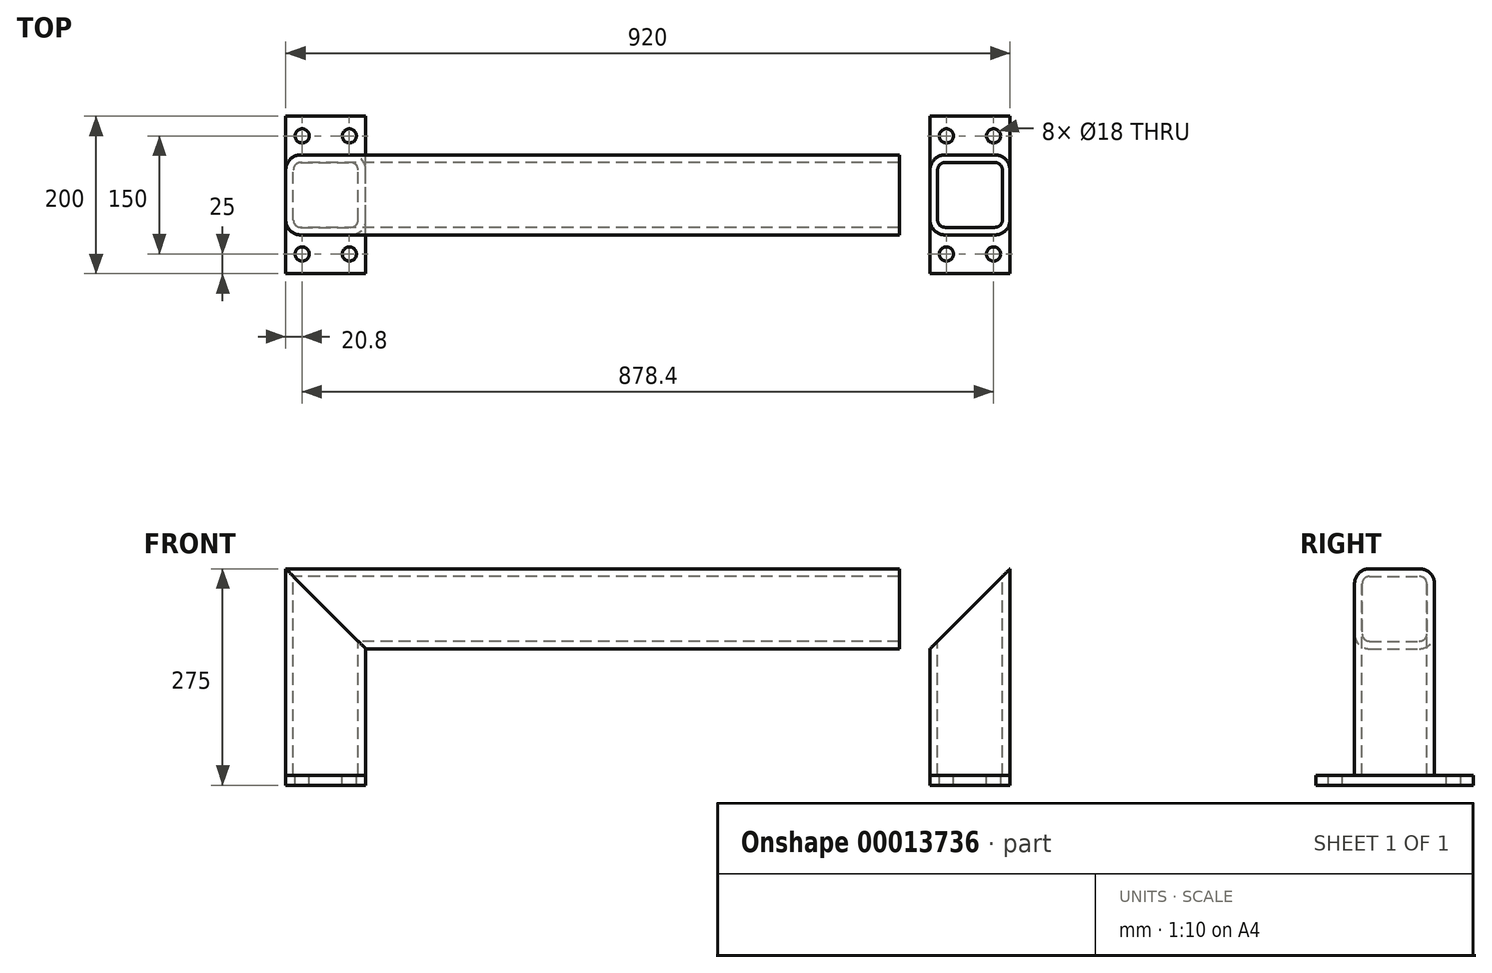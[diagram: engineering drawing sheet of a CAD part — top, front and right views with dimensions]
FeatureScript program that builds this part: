
annotation { "Feature Type Name" : "Feature", "Feature Type Description" : "" }
export const myFeature = defineFeature(function(context is Context, id is Id, definition is map)
    precondition{}
    {
        {
            var Q0;
            Q0=qCreatedBy(makeId("Right.planeOp"),FACE);
            var sketch = newSketch(context, id + "F0", { "sketchPlane" : qUnion([Q0])});
            skLineSegment(sketch, "E0.rect.bottom", {"start": v(-31.8, 50.8) * mm, "end": v(31.8, 50.8) * mm});
            skLineSegment(sketch, "E0.rect.top", {"start": v(-31.8, -50.8) * mm, "end": v(31.8, -50.8) * mm});
            skLineSegment(sketch, "E0.rect.left", {"start": v(-50.8, 31.8) * mm, "end": v(-50.8, -31.8) * mm});
            skLineSegment(sketch, "E0.rect.right", {"start": v(50.8, 31.8) * mm, "end": v(50.8, -31.8) * mm});
            skPoint(sketch, "E0.rect.middle", {"position": v(0, 0) * mm});
            skPoint(sketch, "E1.visualSharp", {"position": v(-50.8, 50.8) * mm});
            skArc(sketch, "E1.filletArc", {"start": v(-31.8, 50.8) * mm, "mid": v(-45.24, 45.24) * mm, "end": v(-50.8, 31.8) * mm});
            skPoint(sketch, "E2.visualSharp", {"position": v(50.8, 50.8) * mm});
            skArc(sketch, "E2.filletArc", {"start": v(50.8, 31.8) * mm, "mid": v(45.24, 45.24) * mm, "end": v(31.8, 50.8) * mm});
            skPoint(sketch, "E3.visualSharp", {"position": v(50.8, -50.8) * mm});
            skArc(sketch, "E3.filletArc", {"start": v(31.8, -50.8) * mm, "mid": v(45.24, -45.24) * mm, "end": v(50.8, -31.8) * mm});
            skPoint(sketch, "E4.visualSharp", {"position": v(-50.8, -50.8) * mm});
            skArc(sketch, "E4.filletArc", {"start": v(-50.8, -31.8) * mm, "mid": v(-45.24, -45.24) * mm, "end": v(-31.8, -50.8) * mm});
            skArc(sketch, "E5.0", {"start": v(-31.8, 41.15) * mm, "mid": v(-38.41, 38.41) * mm, "end": v(-41.15, 31.8) * mm});
            skLineSegment(sketch, "E5.1", {"start": v(-41.15, 31.8) * mm, "end": v(-41.15, -31.8) * mm});
            skArc(sketch, "E5.2", {"start": v(-41.15, -31.8) * mm, "mid": v(-38.41, -38.41) * mm, "end": v(-31.8, -41.15) * mm});
            skLineSegment(sketch, "E5.3", {"start": v(-31.8, -41.15) * mm, "end": v(31.8, -41.15) * mm});
            skArc(sketch, "E5.4", {"start": v(31.8, -41.15) * mm, "mid": v(38.41, -38.41) * mm, "end": v(41.15, -31.8) * mm});
            skLineSegment(sketch, "E5.5", {"start": v(-31.8, 41.15) * mm, "end": v(31.8, 41.15) * mm});
            skLineSegment(sketch, "E5.6", {"start": v(41.15, 31.8) * mm, "end": v(41.15, -31.8) * mm});
            skArc(sketch, "E5.7", {"start": v(41.15, 31.8) * mm, "mid": v(38.41, 38.41) * mm, "end": v(31.8, 41.15) * mm});
            skSolve(sketch);
        }
        {
            var Q0;
            Q0 = qSketchRegion(id + "F0", true);
            extrude(context, id + "F1", {"entities" : qUnion([Q0]), "endBound" : BoundingType.SYMMETRIC, "depth" : 920 * mm});
        }
        {
            var Q0;
            Q0=makeQuery(id+"F1.opExtrude","SWEPT_FACE",FACE,{"disambiguationData":[OSD([sQuery(id+"F0.wireOp",EDGE,"E0.rect.right")])]});
            var sketch = newSketch(context, id + "F2", { "sketchPlane" : qUnion([Q0])});
            skLineSegment(sketch, "E6.0", {"start": v(-460, 50.8) * mm, "end": v(460, 50.8) * mm, "construction": true});
            skLineSegment(sketch, "E7.0", {"start": v(-460, -50.8) * mm, "end": v(460, -50.8) * mm, "construction": true});
            skLineSegment(sketch, "E8", {"start": v(-460, 50.8) * mm, "end": v(-332.27, -76.93) * mm});
            skLineSegment(sketch, "E9.0", {"start": v(-460, 31.8) * mm, "end": v(-460, -31.8) * mm});
            skLineSegment(sketch, "E10", {"start": v(-332.27, -76.93) * mm, "end": v(-460, -76.93) * mm});
            skLineSegment(sketch, "E11", {"start": v(-460, -76.93) * mm, "end": v(-460, 50.8) * mm});
            skLineSegment(sketch, "E12", {"start": v(0, 0) * mm, "end": v(0, -179.73) * mm, "construction": true});
            skLineSegment(sketch, "E13.0.MirrorCS", {"start": v(460, -76.93) * mm, "end": v(460, 50.8) * mm});
            skLineSegment(sketch, "E13.1.MirrorCS", {"start": v(460, 50.8) * mm, "end": v(332.27, -76.93) * mm});
            skLineSegment(sketch, "E13.2.MirrorCS", {"start": v(460, 31.8) * mm, "end": v(460, -31.8) * mm});
            skLineSegment(sketch, "E13.3.MirrorCS", {"start": v(332.27, -76.93) * mm, "end": v(460, -76.93) * mm});
            skSolve(sketch);
        }
        {
            var Q0;
            Q0 = qSketchRegion(id + "F2", true);
            extrude(context, id + "F3", {"entities" : qUnion([Q0]), "operationType" : NewBodyOperationType.REMOVE, "endBound" : BoundingType.THROUGH_ALL, "oppositeDirection" : true, "depth" : 25 * mm});
        }
        {
            var Q0;
            Q0=makeQuery(id+"F1.opExtrude","SWEPT_FACE",FACE,{"disambiguationData":[OSD([sQuery(id+"F0.wireOp",EDGE,"E0.rect.bottom")])]});
            var sketch = newSketch(context, id + "F4", { "sketchPlane" : qUnion([Q0])});
            skLineSegment(sketch, "E14.0", {"start": v(460, -31.8) * mm, "end": v(460, 31.8) * mm});
            skArc(sketch, "E15.0", {"start": v(460, -31.8) * mm, "mid": v(454.44, -45.24) * mm, "end": v(441, -50.8) * mm});
            skArc(sketch, "E16.0", {"start": v(377.4, -50.8) * mm, "mid": v(363.96, -45.24) * mm, "end": v(358.4, -31.8) * mm});
            skLineSegment(sketch, "E17.0", {"start": v(358.4, -31.8) * mm, "end": v(358.4, 31.8) * mm});
            skArc(sketch, "E18.0", {"start": v(358.4, 31.8) * mm, "mid": v(363.96, 45.24) * mm, "end": v(377.4, 50.8) * mm});
            skArc(sketch, "E19.0", {"start": v(441, 50.8) * mm, "mid": v(454.44, 45.24) * mm, "end": v(460, 31.8) * mm});
            skArc(sketch, "E20.0", {"start": v(441, 41.15) * mm, "mid": v(447.61, 38.41) * mm, "end": v(450.35, 31.8) * mm});
            skLineSegment(sketch, "E21.0", {"start": v(450.35, -31.8) * mm, "end": v(450.35, 31.8) * mm});
            skArc(sketch, "E22.0", {"start": v(450.35, -31.8) * mm, "mid": v(447.61, -38.41) * mm, "end": v(441, -41.15) * mm});
            skArc(sketch, "E23.0", {"start": v(377.4, -41.15) * mm, "mid": v(370.79, -38.41) * mm, "end": v(368.05, -31.8) * mm});
            skLineSegment(sketch, "E24.0", {"start": v(368.05, -31.8) * mm, "end": v(368.05, 31.8) * mm});
            skArc(sketch, "E25.0", {"start": v(368.05, 31.8) * mm, "mid": v(370.79, 38.41) * mm, "end": v(377.4, 41.15) * mm});
            skLineSegment(sketch, "E26", {"start": v(441, -50.8) * mm, "end": v(377.4, -50.8) * mm});
            skLineSegment(sketch, "E27", {"start": v(441, -41.15) * mm, "end": v(377.4, -41.15) * mm});
            skLineSegment(sketch, "E28", {"start": v(441, 41.15) * mm, "end": v(377.4, 41.15) * mm});
            skLineSegment(sketch, "E29", {"start": v(441, 50.8) * mm, "end": v(377.4, 50.8) * mm});
            skSolve(sketch);
        }
        {
            var Q0;
            Q0 = qSketchRegion(id + "F4", true);
            extrude(context, id + "F5", {"entities" : qUnion([Q0]), "oppositeDirection" : true, "depth" : (275 - 12.7) * mm});
        }
        {
            var Q0;
            Q0=makeQuery(id+"F5.opExtrude","SWEPT_FACE",FACE,{"disambiguationData":[OSD([sQuery(id+"F4.wireOp",EDGE,"E29")])]});
            var sketch = newSketch(context, id + "F6", { "sketchPlane" : qUnion([Q0])});
            skLineSegment(sketch, "E30.0", {"start": v(-441, 50.8) * mm, "end": v(-460, 50.8) * mm, "construction": true});
            skLineSegment(sketch, "E31.0", {"start": v(-441, 50.8) * mm, "end": v(-377.4, 50.8) * mm, "construction": true});
            skLineSegment(sketch, "E32.0", {"start": v(-358.4, 50.8) * mm, "end": v(-377.4, 50.8) * mm, "construction": true});
            skLineSegment(sketch, "E33.0", {"start": v(-460, -211.5) * mm, "end": v(-460, 50.8) * mm, "construction": true});
            skLineSegment(sketch, "E34.0", {"start": v(-358.4, -211.5) * mm, "end": v(-358.4, 50.8) * mm, "construction": true});
            skLineSegment(sketch, "E35", {"start": v(-460, 50.8) * mm, "end": v(-319.53, -89.67) * mm});
            skLineSegment(sketch, "E36", {"start": v(-319.53, -89.67) * mm, "end": v(-319.53, 50.8) * mm});
            skLineSegment(sketch, "E37", {"start": v(-319.53, 50.8) * mm, "end": v(-460, 50.8) * mm});
            skSolve(sketch);
        }
        {
            var Q0;
            Q0 = qSketchRegion(id + "F6", true);
            extrude(context, id + "F7", {"entities" : qUnion([Q0]), "operationType" : NewBodyOperationType.REMOVE, "endBound" : BoundingType.THROUGH_ALL, "oppositeDirection" : true, "depth" : 25 * mm});
        }
        {
            var Q0;
            Q0=makeQuery(id+"F5.opExtrude","SWEPT_BODY",BODY,{"disambiguationData":[OSD([sQuery(id+"F4.wireOp",EDGE,"E14.0"),sQuery(id+"F4.wireOp",EDGE,"E15.0"),sQuery(id+"F4.wireOp",EDGE,"E16.0"),sQuery(id+"F4.wireOp",EDGE,"E17.0"),sQuery(id+"F4.wireOp",EDGE,"E18.0"),sQuery(id+"F4.wireOp",EDGE,"E19.0"),sQuery(id+"F4.wireOp",EDGE,"E20.0"),sQuery(id+"F4.wireOp",EDGE,"E21.0"),sQuery(id+"F4.wireOp",EDGE,"E22.0"),sQuery(id+"F4.wireOp",EDGE,"E23.0"),sQuery(id+"F4.wireOp",EDGE,"E24.0"),sQuery(id+"F4.wireOp",EDGE,"E25.0"),sQuery(id+"F4.wireOp",EDGE,"E26"),sQuery(id+"F4.wireOp",EDGE,"E27"),sQuery(id+"F4.wireOp",EDGE,"E28"),sQuery(id+"F4.wireOp",EDGE,"E29")])]});
            var Q1;
            Q1=qCreatedBy(makeId("Right.planeOp"),FACE);
            mirror(context, id + "F8", {"entities" : qUnion([Q0]), "mirrorPlane" : qUnion([Q1])});
        }
        {
            var Q0;
            Q0=makeQuery(id+"F5.opExtrude","CAP_FACE",FACE,{"disambiguationData":[OSD([sQuery(id+"F4.wireOp",EDGE,"E14.0"),sQuery(id+"F4.wireOp",EDGE,"E15.0"),sQuery(id+"F4.wireOp",EDGE,"E16.0"),sQuery(id+"F4.wireOp",EDGE,"E17.0"),sQuery(id+"F4.wireOp",EDGE,"E18.0"),sQuery(id+"F4.wireOp",EDGE,"E19.0"),sQuery(id+"F4.wireOp",EDGE,"E20.0"),sQuery(id+"F4.wireOp",EDGE,"E21.0"),sQuery(id+"F4.wireOp",EDGE,"E22.0"),sQuery(id+"F4.wireOp",EDGE,"E23.0"),sQuery(id+"F4.wireOp",EDGE,"E24.0"),sQuery(id+"F4.wireOp",EDGE,"E25.0"),sQuery(id+"F4.wireOp",EDGE,"E26"),sQuery(id+"F4.wireOp",EDGE,"E27"),sQuery(id+"F4.wireOp",EDGE,"E28"),sQuery(id+"F4.wireOp",EDGE,"E29")])],"isStart":false});
            var sketch = newSketch(context, id + "F9", { "sketchPlane" : qUnion([Q0])});
            skLineSegment(sketch, "E38", {"start": v(409.2, -100) * mm, "end": v(409.2, 100) * mm, "construction": true});
            skLineSegment(sketch, "E39", {"start": v(460, 0) * mm, "end": v(358.4, 0) * mm, "construction": true});
            skLineSegment(sketch, "E40.0", {"start": v(460, -100) * mm, "end": v(358.4, -100) * mm});
            skLineSegment(sketch, "E41.0.MirrorCS", {"start": v(460, 100) * mm, "end": v(358.4, 100) * mm});
            skLineSegment(sketch, "E42", {"start": v(460, -100) * mm, "end": v(460, 100) * mm});
            skLineSegment(sketch, "E43", {"start": v(358.4, 100) * mm, "end": v(358.4, -100) * mm});
            skPoint(sketch, "E44.orphan", {"position": v(409.2, -50.8) * mm});
            skPoint(sketch, "E45.orphan", {"position": v(409.2, 50.8) * mm});
            skLineSegment(sketch, "E46.0", {"start": v(439.2, -102.5) * mm, "end": v(439.2, 102.5) * mm, "construction": true});
            skLineSegment(sketch, "E47.0", {"start": v(450, -75) * mm, "end": v(348.4, -75) * mm, "construction": true});
            skCircle(sketch, "E48", {"center": v(439.2, -75) * mm, "radius": 9 * mm});
            skCircle(sketch, "E49.0.MirrorC", {"center": v(379.2, -75) * mm, "radius": 9 * mm});
            skCircle(sketch, "E50.0.MirrorC", {"center": v(439.2, 75) * mm, "radius": 9 * mm});
            skCircle(sketch, "E51.0.MirrorC", {"center": v(379.2, 75) * mm, "radius": 9 * mm});
            skSolve(sketch);
        }
        {
            var Q0;
            Q0 = qSketchRegion(id + "F9", true);
            extrude(context, id + "F10", {"entities" : qUnion([Q0]), "depth" : 12.7 * mm});
        }
        {
            var Q0;
            Q0=makeQuery(id+"F10.opExtrude","SWEPT_BODY",BODY,{"disambiguationData":[OSD([sQuery(id+"F9.wireOp",EDGE,"E40.0"),sQuery(id+"F9.wireOp",EDGE,"E41.0.MirrorCS"),sQuery(id+"F9.wireOp",EDGE,"E42"),sQuery(id+"F9.wireOp",EDGE,"E43"),sQuery(id+"F9.wireOp",EDGE,"E48"),sQuery(id+"F9.wireOp",EDGE,"E49.0.MirrorC"),sQuery(id+"F9.wireOp",EDGE,"E50.0.MirrorC"),sQuery(id+"F9.wireOp",EDGE,"E51.0.MirrorC")])]});
            var Q1;
            Q1=qCreatedBy(makeId("Right.planeOp"),FACE);
            mirror(context, id + "F11", {"entities" : qUnion([Q0]), "mirrorPlane" : qUnion([Q1])});
        }
    });
